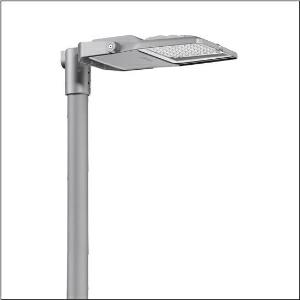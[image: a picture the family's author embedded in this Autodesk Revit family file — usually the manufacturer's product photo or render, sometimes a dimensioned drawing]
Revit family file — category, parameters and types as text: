
# Revit family: floodlight_fl_21_mini___pl33t_5xa7775d2f3a_2fb5
name_source: partatom
category: Lighting Fixtures
units: mm (PartAtom-declared; Revit-internal decimal feet)

## family parameters
Cut with Voids When Loaded = No
Host = Face
Light Source = No
Part Type = Normal
Room Calculation Point = No
Round Connector Dimension = Use Diameter
Shared = No

## types (1)
- --- (1 x LED, 17630 lm, 142.9 W, 3000K)
    Apparent Load = 143 VA
    CIE Flux Codes = 26 75 99 100 100
    Color Rendering = 70
    Color Temperature = 3000K
    Default Elevation = 1800 mm
    Description = Floodlight FL 21 mini, floodlight, primary light control with lens, of PMMA, primary optical cover: protective disc, of toughened safety glass, transparent, light distribution: PL33T, light emission: direct distribution, installation type: surface-mounted, LED, High Power LED, rated luminous flux: 17.630lm, luminous efficacy: 123lm/W, light colour: 730, colour temperature: 3000K, control gear: Smart Interface (Zhaga), control: flexible luminous flux parameterisation, time-dependent luminous flux control, constant luminous flux control, overheat protection, pre-setting: logarithmic dimming characteristic, with terminal, 6-pole, mains connection: 220..240V, AC, 50/60Hz, start of lifetime: 143W, end of service life: 151W, reduction: 63W, luminaire housing, of diecast aluminium, powder-coated, SITECO metallic grey (DB 702S), corrosivity category C5 mid according to DIN EN ISO 12944, suitable for swimming pools, chlorine-resistant, sealing non-destructively replaceable, please order mast flange separately, mast bracket, of steel, galvanised, powder-coated, SITECO metallic grey (DB 702S), Smart Interface above, protection rating (complete): IP66, insulation class (complete): insulation class II (safety insulation), certification: CE, ENEC, VDE, protection symbol: D, impact resistance: IK08, permissible operating ambient temperature: -40..+40°C, permissible operating ambient temperature for outdoor applications: -40..+50°C, standard: DIN EN 12944, LABS conformity tested according to VDMA 24364:2018-05, packaging unit: 1 piece

Light Distribution: PL33T
    Height = 70 mm
    Lamp = 1 x LED
    Lamp Light Flux = 17630 lm
    Lamp Power = 142.9 W
    Lamp count = 1
    Length = 485 mm
    Luminous efficacy = 123 lm/W
    Manufacturer = Siteco
    ModVariant = No
    Model = 5XA7775D2F3A
    Mounting Place = Pole
    Mounting Type = Pole annexe
    Number of Poles = 1
    OnlyDefault = Yes
    Power Factor = 1
    Product Name = Floodlight FL 21 mini | PL33T
    Product group = floodlight | pylon annexe
    ProductGroupID = 6201
    Protection Class = Protection class II
    Protection Degree = IP 66
    RLX_Detail_Level = 1
    RLX_Emergency_Light_Flux = 0 lm
    RLX_Emergency_Type = 0
    RLX_Emergency_Type_DB = No
    RlxData = <blob elided: 101201 chars, md5=d87e38d0>
    Socket = socket
    Standby Power = 0 W
    System Light Flux = 17630 lm
    System Power = 143 W
    Type Comments = factory setting: luminous flux: 100 % | dim-lin: 254 | 730 mA
    Type Image = l_1007125.jpg
    URL = http://relux.com
    VarID = @adj_149449
    Voltage = 0 V
    Weight = 0.00 kg
    Width = 337 mm

## geometry (parser evidence)
native form markers: Blend x4, Sweep x14
no freeform markers — native parametric forms only
